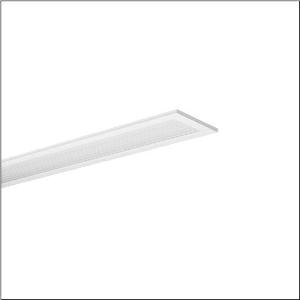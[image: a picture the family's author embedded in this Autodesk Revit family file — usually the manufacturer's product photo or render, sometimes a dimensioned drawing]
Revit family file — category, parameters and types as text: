
# Revit family: apollon_r__21_linear_51mq16wd2414_c89d
name_source: partatom
category: Lighting Fixtures
units: mm (PartAtom-declared; Revit-internal decimal feet)

## family parameters
Cut with Voids When Loaded = No
Host = Face
Light Source = No
Part Type = Normal
Room Calculation Point = No
Round Connector Dimension = Use Diameter
Shared = No

## types (1)
- Apollon® 21 linear (1 x LED, 3400 lm, 23.2 W, 4000K)
    Apparent Load = 23 VA
    CIE Flux Codes = 64 88 97 100 100
    Color Rendering = 80
    Color Temperature = 4000K
    Default Elevation = 1800 mm
    Description = Apollon® 21 linear, office luminaire, primary optical cover: micro prismatic cover, of PMMA, CAT 2 (L<= 3000cd/m²), light emission: direct distribution, primary light characteristic: symmetric, installation type: lay-in mounting, LED, rated luminous flux: 3.400lm, luminous efficacy: 147lm/W, light colour: 840, colour temperature: 4000K, with terminal, 5-pole, mains connection: 220..240V, AC/DC, 0/50..60Hz, rated input power: 23.2W, housing, of aluminium, coated, traffic white (RAL 9016), length: 1.545mm, width: 179mm, height: 30mm, housing upper side, of sheet steel, galvanised, protection rating (complete): IP20, protection rating (lamp compartment, on room side): IP50, insulation class (complete): insulation class II (safety insulation), certification: CE, ENEC, impact resistance: IK03, permissible operating ambient temperature: -20..+45°C, permissible storage temperature: -40..+80°C, packaging unit: 1 piece
    Height = 0 mm  [stored 0 ft]
    Lamp = 1 x LED
    Lamp Light Flux = 3400 lm
    Lamp Power = 23.2 W
    Lamp count = 1
    Length = 1545 mm
    Luminous efficacy = 147 lm/W
    Manufacturer = Siteco
    ModVariant = No
    Model = 51MQ16WD2414
    Mounting Place = Ceiling
    Mounting Type = Recessed
    Number of Poles = 1
    OnlyDefault = Yes
    Power Factor = 1
    Product Name = Apollon® 21 linear
    Product group = office luminaire | ceiling recessed
    ProductGroupID = 401
    Protection Class = Protection class II
    Protection Degree = IP 20
    RLX_Detail_Level = 1
    RLX_Emergency_Light_Flux = 0 lm
    RLX_Emergency_Type = 0
    RLX_Emergency_Type_DB = No
    RlxData = <blob elided: 12553 chars, md5=7a379a70>
    Socket = socket
    Standby Power = 0 W
    System Light Flux = 3400 lm
    System Power = 23 W
    Type Comments = Product without accessories
    Type Image = l_1291018.jpg
    URL = http://relux.com
    VarID = ---
    Voltage = 0 V
    Weight = 0.00 kg
    Width = 179 mm

note: [stored X ft] marks values corroborated as IEEE doubles in the binary element streams (Revit-internal decimal feet)

## geometry (parser evidence)
native form markers: Sweep x8
no freeform markers — native parametric forms only
